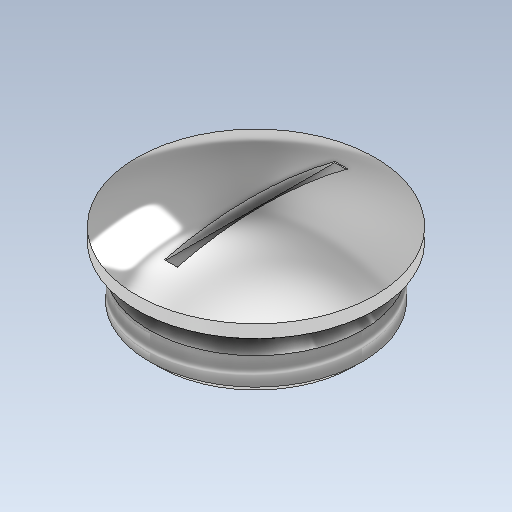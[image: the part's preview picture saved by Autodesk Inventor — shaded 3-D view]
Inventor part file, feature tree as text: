
AUTODESK INVENTOR PART (.ipt)
format: ipt  version: 2021 (Build 250183000, 183)  size: 196,608 bytes
history: native  units: mm
features: sketch x6, extrude x5, chamfer x2, thread x1, revolve x1
ambient origin geometry x8: Origin, YZ Plane, XZ Plane, XY Plane, X Axis, Y Axis, Z Axis, Center Point
bodies: Solid1 (feature_tree)
feature tree (15):
  extrude  "Extrusion1"  Depth=1.5mm TaperAngle=0.0deg
  extrude  "Extrusion2"  Depth=1.8mm TaperAngle=0.0deg
  extrude  "Extrusion3"  Depth=5.2mm TaperAngle=0.0deg
  chamfer  "Chamfer1"  Distance=1.0mm Angle=45.0deg
  thread  "Thread1"  [1 undecoded]
  revolve  "Revolution1"  Angle=90.0deg
  extrude  "Extrusion4"  Depth=20.0mm TaperAngle=0.0deg
  extrude  "Extrusion5"  Depth=7.5mm TaperAngle=0.0deg
  chamfer  "Chamfer2"  Distance=0.5mm Angle=45.0deg
  sketch  "Sketch1"  dims[d0=28.0mm d1=1.5mm d2=0.0mm]
  sketch  "Sketch2"  dims[d3=22.0mm d4=1.8mm d5=0.0mm]
  sketch  "Sketch3"  dims[d6=25.0mm d7=5.2mm d8=0.0mm d9=1.0mm d10=2.0mm d11=45.0deg d12=3.2mm d13=0.0mm]
  sketch  "Sketch4"  dims[d15=11.0mm d16=90.0deg]
  sketch  "Sketch5"  dims[d17=1.5mm d18=20.0mm d19=0.0mm]
  sketch  "Sketch6"  dims[d20=20.0mm d21=7.5mm d22=0.0mm d23=0.5mm d24=2.0mm d25=45.0deg]
note: 1 required parameter value undecoded (feature->parameter linkage not recoverable at this tier; creation-order binding heuristic only, values carry confidence <= 0.55)
